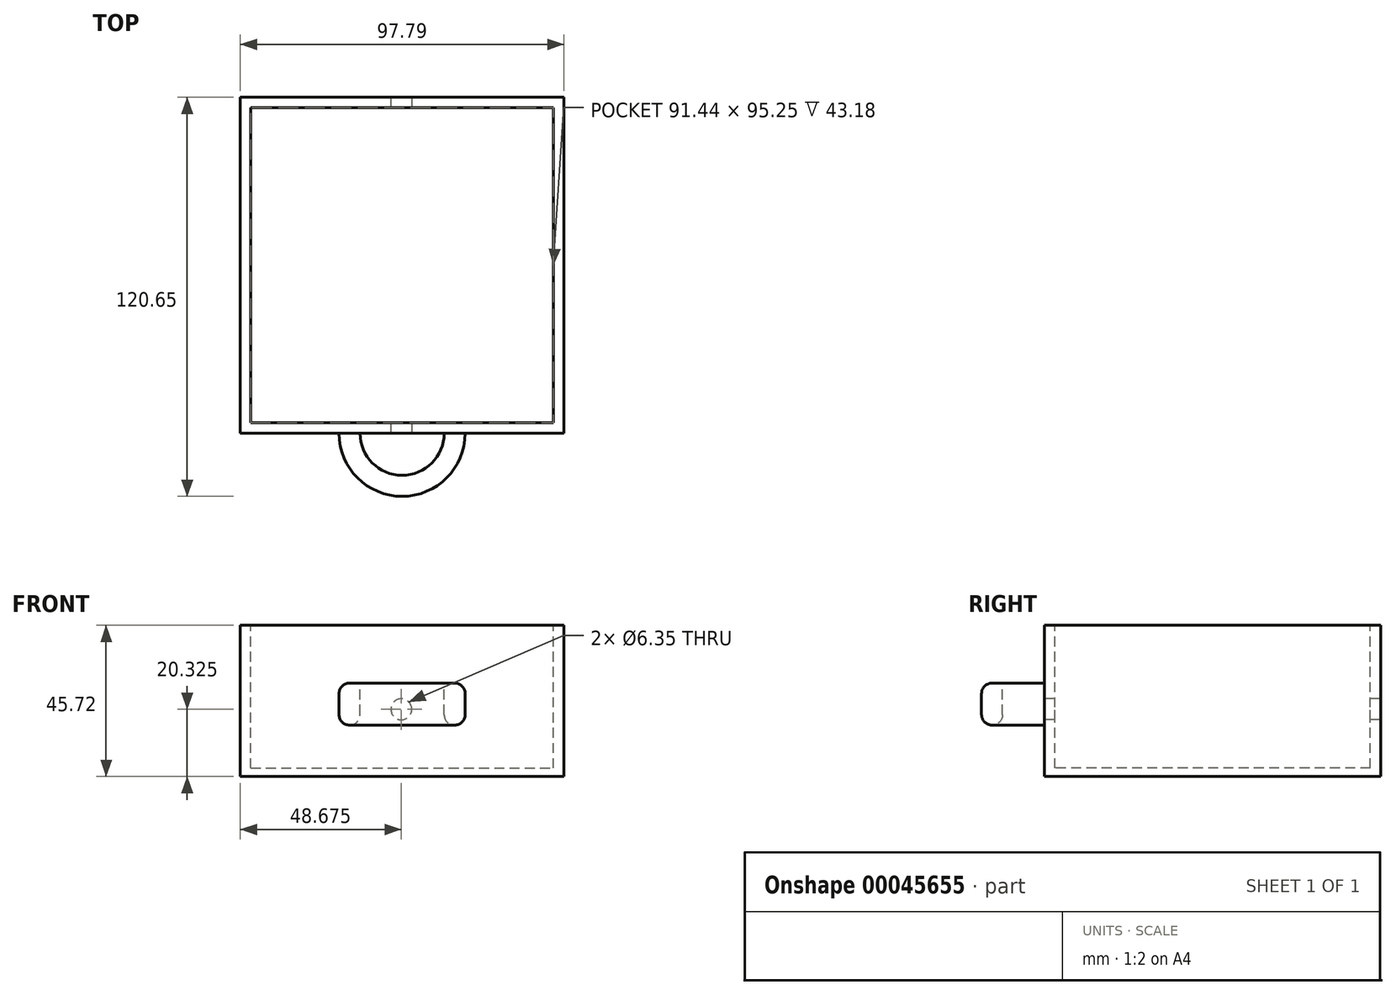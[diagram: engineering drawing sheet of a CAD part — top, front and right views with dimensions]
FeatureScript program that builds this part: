
annotation { "Feature Type Name" : "Feature", "Feature Type Description" : "" }
export const myFeature = defineFeature(function(context is Context, id is Id, definition is map)
    precondition{}
    {
        {
            var Q0;
            Q0=qCreatedBy(makeId("Front.planeOp"),FACE);
            var sketch = newSketch(context, id + "F0", { "sketchPlane" : qUnion([Q0])});
            skLineSegment(sketch, "E0.bottom", {"start": v(-33.41, 27.52) * mm, "end": v(64.38, 27.52) * mm});
            skLineSegment(sketch, "E0.top", {"start": v(-33.41, -18.2) * mm, "end": v(64.38, -18.2) * mm});
            skLineSegment(sketch, "E0.left", {"start": v(-33.41, 27.52) * mm, "end": v(-33.41, -18.2) * mm});
            skLineSegment(sketch, "E0.right", {"start": v(64.38, 27.52) * mm, "end": v(64.38, -18.2) * mm});
            skSolve(sketch);
        }
        {
            var Q0;
            Q0=qSketchRegion(id+"F0",true);
            extrude(context, id + "F1", {"entities" : qUnion([Q0]), "oppositeDirection" : true, "depth" : 101.6 * mm});
        }
        {
            var Q0;
            Q0=makeQuery(id+"F1.opExtrude","SWEPT_FACE",FACE,{"disambiguationData":[OSD([sQuery(id+"F0.wireOp",EDGE,"E0.bottom")])]});
            var sketch = newSketch(context, id + "F2", { "sketchPlane" : qUnion([Q0])});
            skLineSegment(sketch, "E1.bottom", {"start": v(-30.24, 98.43) * mm, "end": v(61.2, 98.43) * mm});
            skLineSegment(sketch, "E1.top", {"start": v(-30.24, 3.17) * mm, "end": v(61.2, 3.18) * mm});
            skLineSegment(sketch, "E1.left", {"start": v(-30.24, 98.43) * mm, "end": v(-30.24, 3.17) * mm});
            skLineSegment(sketch, "E1.right", {"start": v(61.2, 98.43) * mm, "end": v(61.2, 3.18) * mm});
            skSolve(sketch);
        }
        {
            var Q0;
            Q0=qSketchRegion(id+"F2",true);
            extrude(context, id + "F3", {"entities" : qUnion([Q0]), "operationType" : NewBodyOperationType.REMOVE, "oppositeDirection" : true, "depth" : 43.18 * mm});
        }
        {
            var Q0;
            Q0=makeQuery(id+"F1.opExtrude","CAP_FACE",FACE,{"disambiguationData":[OSD([sQuery(id+"F0.wireOp",EDGE,"E0.bottom"),sQuery(id+"F0.wireOp",EDGE,"E0.top"),sQuery(id+"F0.wireOp",EDGE,"E0.left"),sQuery(id+"F0.wireOp",EDGE,"E0.right")])],"isStart":true});
            var sketch = newSketch(context, id + "F4", { "sketchPlane" : qUnion([Q0])});
            skLineSegment(sketch, "E2.bottom", {"start": v(-3.57, 10.06) * mm, "end": v(34.53, 10.06) * mm});
            skLineSegment(sketch, "E2.top", {"start": v(-3.57, -2.64) * mm, "end": v(34.53, -2.64) * mm});
            skLineSegment(sketch, "E2.left", {"start": v(-3.57, 10.06) * mm, "end": v(-3.57, -2.64) * mm});
            skLineSegment(sketch, "E2.right", {"start": v(34.53, 10.06) * mm, "end": v(34.53, -2.64) * mm});
            skLineSegment(sketch, "E3", {"start": v(-3.57, 3.71) * mm, "end": v(34.53, 3.71) * mm});
            skLineSegment(sketch, "E4", {"start": v(15.48, 10.06) * mm, "end": v(15.48, -2.64) * mm});
            skPoint(sketch, "E5", {"position": v(15.48, 3.71) * mm});
            skPoint(sketch, "E6", {"position": v(15.48, -18.2) * mm});
            skSolve(sketch);
        }
        {
            var Q0;
            {var subQ3=sQuery(id+"F4.wireOp",EDGE,"E2.bottom");var subQ5=sQuery(id+"F4.wireOp",EDGE,"E2.left");var subQ7=makeQuery(id+"F4.imprint","INTERSECT",VERTEX,{"derivedFrom":[subQ3,subQ5]});Q0=makeQuery(id+"F4.imprint","IMPRINT",FACE,{"disambiguationData":[TD([[makeQuery(id+"F4.imprint","IMPRINT",EDGE,{"disambiguationData":[TD([[subQ7,-1.0]])],"derivedFrom":subQ3}),-1.0]])]});}
            var Q1;
            {var subQ3=sQuery(id+"F4.wireOp",EDGE,"E2.top");var subQ5=sQuery(id+"F4.wireOp",EDGE,"E2.left");var subQ7=makeQuery(id+"F4.imprint","INTERSECT",VERTEX,{"derivedFrom":[subQ3,subQ5]});Q1=makeQuery(id+"F4.imprint","IMPRINT",FACE,{"disambiguationData":[TD([[makeQuery(id+"F4.imprint","IMPRINT",EDGE,{"disambiguationData":[TD([[subQ7,-1.0]])],"derivedFrom":subQ3}),1.0]])]});}
            var Q2;
            Q2=sQuery(id+"F4.wireOp",EDGE,"E4");
            revolve(context, id + "F5", {"operationType" : NewBodyOperationType.ADD, "entities" : qUnion([Q0, Q1]), "axis" : qUnion([Q2]), "revolveType" : RevolveType.ONE_DIRECTION, "oppositeDirection" : true, "angle" : 180 * degree});
        }
        {
            var Q0;
            Q0=makeQuery(id+"F5.opRevolve","SWEPT_FACE",FACE,{"disambiguationData":[OSD([sQuery(id+"F4.wireOp",EDGE,"E2.bottom")])]});
            var sketch = newSketch(context, id + "F6", { "sketchPlane" : qUnion([Q0])});
            skLineSegment(sketch, "E7", {"start": v(2.78, 0) * mm, "end": v(28.18, 0) * mm});
            skArc(sketch, "E8", {"start": v(2.78, 0) * mm, "mid": v(15.48, -12.7) * mm, "end": v(28.18, 0) * mm});
            skSolve(sketch);
        }
        {
            var Q0;
            Q0=qSketchRegion(id+"F6",true);
            extrude(context, id + "F7", {"entities" : qUnion([Q0]), "operationType" : NewBodyOperationType.REMOVE, "oppositeDirection" : true, "depth" : 25.4 * mm});
        }
        {
            var Q0;
            Q0=makeQuery(id+"F5.opRevolve","SWEPT_EDGE",EDGE,{"disambiguationData":[OSD([sQuery(id+"F4.wireOp",EDGE,"E2.bottom"),sQuery(id+"F4.wireOp",EDGE,"E2.left")])]});
            var Q1;
            Q1=makeQuery(id+"F7.boolean.opBoolean","COPY",EDGE,{"derivedFrom":makeQuery(id+"F7.opExtrude","CAP_EDGE",EDGE,{"disambiguationData":[OSD([sQuery(id+"F6.wireOp",EDGE,"E8")])],"isStart":true})});
            var Q2;
            Q2=makeQuery(id+"F5.opRevolve","SWEPT_EDGE",EDGE,{"disambiguationData":[OSD([sQuery(id+"F4.wireOp",EDGE,"E2.top"),sQuery(id+"F4.wireOp",EDGE,"E2.left")])]});
            var Q3;
            Q3=makeQuery(id+"F7.boolean.opBoolean","INTERSECT",EDGE,{"derivedFrom":[makeQuery(id+"F5.opRevolve","SWEPT_FACE",FACE,{"disambiguationData":[OSD([sQuery(id+"F4.wireOp",EDGE,"E2.top")])]}),makeQuery(id+"F7.opExtrude","SWEPT_FACE",FACE,{"disambiguationData":[OSD([sQuery(id+"F6.wireOp",EDGE,"E8")])]})]});
            fillet(context, id + "F8", {"entities" : qUnion([Q0, Q1, Q2, Q3]), "radius" : 3.17 * mm, "tangentPropagation" : true, "allowEdgeOverflow" : false});
        }
        {
            var Q0;
            Q0=makeQuery(id+"F7.boolean.opBoolean","MERGE",FACE,{"derivedFrom":[makeQuery(id+"F1.opExtrude","CAP_FACE",FACE,{"disambiguationData":[OSD([sQuery(id+"F0.wireOp",EDGE,"E0.bottom"),sQuery(id+"F0.wireOp",EDGE,"E0.top"),sQuery(id+"F0.wireOp",EDGE,"E0.left"),sQuery(id+"F0.wireOp",EDGE,"E0.right")])],"isStart":true}),makeQuery(id+"F7.opExtrude","SWEPT_FACE",FACE,{"disambiguationData":[OSD([sQuery(id+"F6.wireOp",EDGE,"E7")])]})]});
            var sketch = newSketch(context, id + "F9", { "sketchPlane" : qUnion([Q0])});
            skPoint(sketch, "E9", {"position": v(15.27, 2.12) * mm});
            skSolve(sketch);
        }
        {
            var Q0;
            Q0=sQuery(id+"F9.wireOp",VERTEX,"E9");
            var Q1;
            Q1=makeQuery(id+"F1.opExtrude","SWEPT_BODY",BODY,{"disambiguationData":[OSD([sQuery(id+"F0.wireOp",EDGE,"E0.bottom"),sQuery(id+"F0.wireOp",EDGE,"E0.top"),sQuery(id+"F0.wireOp",EDGE,"E0.left"),sQuery(id+"F0.wireOp",EDGE,"E0.right")])]});
            hole(context, id + "F10", {"style" : HoleStyle.SIMPLE, "holeDiameter" : 6.35 * mm, "endStyle" : HoleEndStyle.THROUGH, "locations" : qUnion([Q0]), "scope" : qUnion([Q1])});
        }
    });
